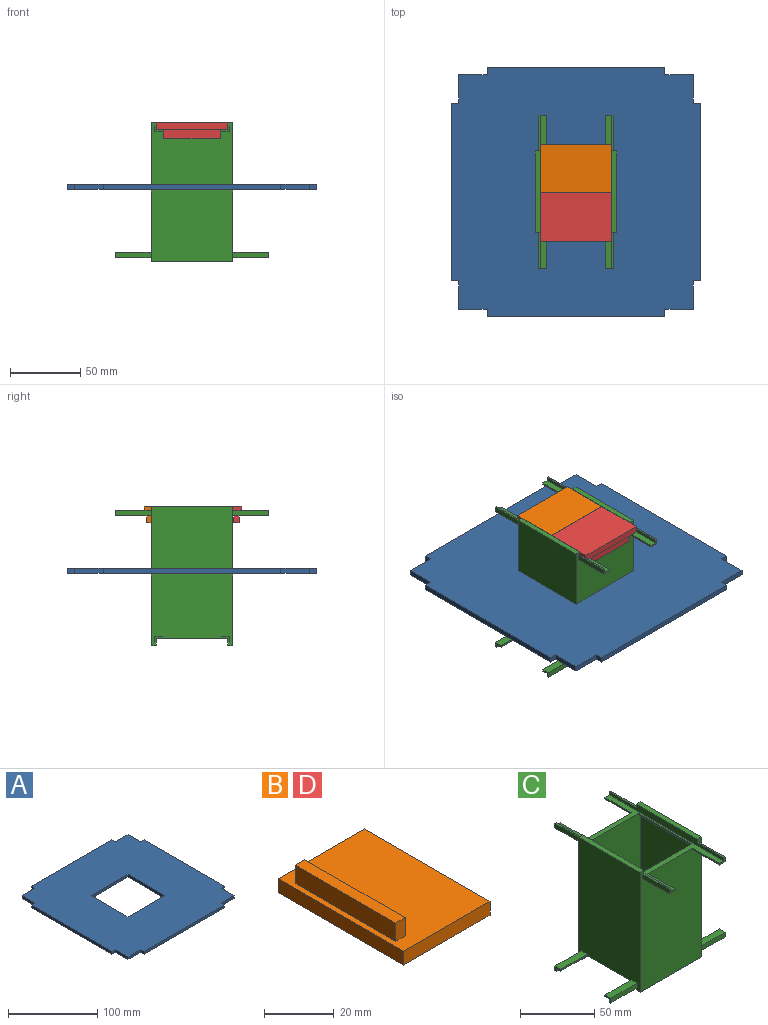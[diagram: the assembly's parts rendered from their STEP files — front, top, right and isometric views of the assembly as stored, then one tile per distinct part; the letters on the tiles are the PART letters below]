
ASSEMBLY  parts=4 mates=6
PART A: 26 faces, bbox 177.8x177.8x3.8 mm
  f0: plane 58.42x3.81mm, normal (0,1,0), area 222.6mm2, adj f1,f23,f24,f25
  f1: plane 58.42x3.81mm, normal (1,0,0), area 222.6mm2, adj f0,f2,f24,f25
  f2: plane 58.42x3.81mm, normal (0,-1,0), area 222.6mm2, adj f1,f23,f24,f25
  f3: plane 5.08x3.81mm, normal (0,-1,0), area 19.4mm2, adj f4,f22,f24,f25
  f4: plane 20.32x3.81mm, normal (-1,0,0), area 77.4mm2, adj f3,f5,f24,f25
  f5: plane 20.32x3.81mm, normal (0,-1,0), area 77.4mm2, adj f4,f6,f24,f25
  f6: plane 5.08x3.81mm, normal (-1,0,0), area 19.4mm2, adj f5,f7,f24,f25
  f7: plane 127x3.81mm, normal (0,-1,0), area 483.9mm2, adj f6,f8,f24,f25
  f8: plane 5.08x3.81mm, normal (1,0,0), area 19.4mm2, adj f7,f9,f24,f25
  f9: plane 20.32x3.81mm, normal (0,-1,0), area 77.4mm2, adj f8,f10,f24,f25
  f10: plane 20.32x3.81mm, normal (1,0,0), area 77.4mm2, adj f9,f11,f24,f25
  f11: plane 5.08x3.81mm, normal (0,-1,0), area 19.4mm2, adj f10,f12,f24,f25
  f12: plane 127x3.81mm, normal (1,0,0), area 483.9mm2, adj f11,f13,f24,f25
  f13: plane 5.08x3.81mm, normal (0,1,0), area 19.4mm2, adj f12,f14,f24,f25
  f14: plane 20.32x3.81mm, normal (1,0,0), area 77.4mm2, adj f13,f15,f24,f25
  f15: plane 20.32x3.81mm, normal (0,1,0), area 77.4mm2, adj f14,f16,f24,f25
  f16: plane 5.08x3.81mm, normal (1,0,0), area 19.4mm2, adj f15,f17,f24,f25
  f17: plane 127x3.81mm, normal (0,1,0), area 483.9mm2, adj f16,f18,f24,f25
  f18: plane 5.08x3.81mm, normal (-1,0,0), area 19.4mm2, adj f17,f19,f24,f25
  f19: plane 20.32x3.81mm, normal (0,1,0), area 77.4mm2, adj f18,f20,f24,f25
  f20: plane 20.32x3.81mm, normal (-1,0,0), area 77.4mm2, adj f19,f21,f24,f25
  f21: plane 5.08x3.81mm, normal (0,1,0), area 19.4mm2, adj f20,f22,f24,f25
  f22: plane 127x3.81mm, normal (-1,0,0), area 483.9mm2, adj f3,f21,f24,f25
  f23: plane 58.42x3.81mm, normal (-1,0,0), area 222.6mm2, adj f0,f2,f24,f25
  f24: plane 177.8x177.8mm, normal (0,0,1), area 27270.9mm2, adj f0,f1,f2,f3,f4,f5,f6,f7
  f25: plane 177.8x177.8mm, normal (0,0,-1), area 27270.9mm2, adj f0,f1,f2,f3,f4,f5,f6,f7
PART B: 11 faces, bbox 34.9x50.8x11.2 mm
  f0: plane 40.64x6.35mm, normal (1,0,0), area 258.1mm2, adj f1,f7,f9,f10
  f1: plane 40.64x3.81mm, normal (0,0,1), area 154.8mm2, adj f0,f4,f9,f10
  f2: plane 34.93x4.83mm, normal (0,-1,0), area 168.5mm2, adj f5,f6,f7,f8
  f3: plane 34.93x4.83mm, normal (0,1,0), area 168.5mm2, adj f5,f6,f7,f8
  f4: plane 40.64x6.35mm, normal (-1,0,0), area 258.1mm2, adj f1,f7,f9,f10
  f5: plane 50.8x4.83mm, normal (-1,0,0), area 245.2mm2, adj f2,f3,f7,f8
  f6: plane 50.8x4.83mm, normal (1,0,0), area 245.2mm2, adj f2,f3,f7,f8
  f7: plane 50.8x34.93mm, normal (0,0,1), area 1619.4mm2, adj f0,f2,f3,f4,f5,f6,f9,f10
  f8: plane 50.8x34.93mm, normal (0,0,-1), area 1774.2mm2, adj f2,f3,f5,f6
  f9: plane 6.35x3.81mm, normal (0,1,0), area 24.2mm2, adj f0,f1,f4,f7
  f10: plane 6.35x3.81mm, normal (0,-1,0), area 24.2mm2, adj f0,f1,f4,f7
PART C: 66 faces, bbox 109.2x109.2x99.1 mm
  f0: plane 99.06x58.42mm, normal (0,-1,0), area 5508.4mm2, adj f2,f3,f9,f10,f11,f14,f15,f16
  f1: plane 99.06x58.42mm, normal (0,1,0), area 5508.4mm2, adj f2,f3,f9,f10,f11,f14,f15,f17
  f2: plane 99.06x58.42mm, normal (-1,0,0), area 5508.4mm2, adj f0,f1,f5,f6,f13,f14,f16,f17
  f3: plane 99.06x58.42mm, normal (1,0,0), area 5508.4mm2, adj f0,f1,f5,f6,f13,f15,f16,f17
  f4: plane 87.63x50.8mm, normal (-1,0,0), area 4448.4mm2, adj f7,f8,f13,f20,f22,f23,f24,f25
  f5: plane 109.22x5.08mm, normal (0,1,0), area 425.8mm2, adj f2,f3,f13,f16,f26,f30,f43,f45
  f6: plane 109.22x5.08mm, normal (0,-1,0), area 425.8mm2, adj f2,f3,f13,f17,f33,f35,f36,f40
  f7: plane 87.63x50.8mm, normal (0,-1,0), area 4447.7mm2, adj f4,f10,f12,f18,f19,f20,f21,f22
  f8: plane 87.63x50.8mm, normal (0,1,0), area 4447.7mm2, adj f4,f10,f12,f18,f19,f20,f21,f24
  f9: plane 109.22x5.08mm, normal (1,0,0), area 425.8mm2, adj f0,f1,f10,f14,f54,f55,f56,f60
  f10: plane 109.22x50.8mm, normal (0,0,1), area 980.6mm2, adj f0,f1,f7,f8,f9,f11,f19,f21
  f11: plane 109.22x5.08mm, normal (-1,0,0), area 425.8mm2, adj f0,f1,f10,f15,f46,f50,f64,f65
  f12: plane 87.63x50.8mm, normal (1,0,0), area 4448.4mm2, adj f7,f8,f13,f18,f22,f23,f24,f25
  f13: plane 109.22x50.8mm, normal (0,0,-1), area 954.8mm2, adj f2,f3,f4,f5,f6,f12,f23,f25
  f14: plane 58.42x3.81mm, normal (0,0,1), area 222.6mm2, adj f0,f1,f2,f9
  f15: plane 58.42x3.81mm, normal (0,0,1), area 222.6mm2, adj f0,f1,f3,f11
  f16: plane 58.42x3.81mm, normal (0,0,-1), area 222.6mm2, adj f0,f2,f3,f5
  f17: plane 58.42x3.81mm, normal (0,0,-1), area 222.6mm2, adj f1,f2,f3,f6
  f18: plane 50.8x1.78mm, normal (0,0,-1), area 90.3mm2, adj f7,f8,f12,f19
  f19: plane 50.8x1.27mm, normal (1,0,0), area 64.5mm2, adj f7,f8,f10,f18
  f20: plane 50.8x1.27mm, normal (0,0,-1), area 64.5mm2, adj f4,f7,f8,f21
  f21: plane 50.8x1.27mm, normal (-1,0,0), area 64.5mm2, adj f7,f8,f10,f20
  f22: plane 50.8x1.27mm, normal (0,0,1), area 64.5mm2, adj f4,f7,f12,f23
  f23: plane 50.8x1.27mm, normal (0,-1,0), area 64.5mm2, adj f4,f12,f13,f22
  f24: plane 50.8x1.27mm, normal (0,0,1), area 64.5mm2, adj f4,f8,f12,f25
  f25: plane 50.8x1.27mm, normal (0,1,0), area 64.5mm2, adj f4,f12,f13,f24
  f26: plane 25.4x1.27mm, normal (0,0,-1), area 32.3mm2, adj f3,f5,f29,f30
  f27: plane 25.4x1.27mm, normal (0,1,0), area 32.3mm2, adj f3,f13,f28,f30
  f28: plane 25.4x5.59mm, normal (0,0,1), area 141.9mm2, adj f3,f27,f29,f30
  f29: plane 25.4x3.81mm, normal (0,-1,0), area 96.8mm2, adj f3,f26,f28,f30
  f30: plane 5.59x3.81mm, normal (1,0,0), area 10.3mm2, adj f5,f13,f26,f27,f28,f29
  f31: plane 25.4x5.59mm, normal (0,0,1), area 141.9mm2, adj f3,f32,f34,f35
  f32: plane 25.4x1.27mm, normal (0,-1,0), area 32.3mm2, adj f3,f13,f31,f35
  f33: plane 25.4x1.27mm, normal (0,0,-1), area 32.3mm2, adj f3,f6,f34,f35
  f34: plane 25.4x3.81mm, normal (0,1,0), area 96.8mm2, adj f3,f31,f33,f35
  f35: plane 5.59x3.81mm, normal (1,0,0), area 10.3mm2, adj f6,f13,f31,f32,f33,f34
  f36: plane 25.4x1.27mm, normal (0,0,-1), area 32.3mm2, adj f2,f6,f39,f40
  f37: plane 25.4x1.27mm, normal (0,-1,0), area 32.3mm2, adj f2,f13,f38,f40
  f38: plane 25.4x5.59mm, normal (0,0,1), area 141.9mm2, adj f2,f37,f39,f40
  f39: plane 25.4x3.81mm, normal (0,1,0), area 96.8mm2, adj f2,f36,f38,f40
  f40: plane 5.59x3.81mm, normal (-1,0,0), area 10.3mm2, adj f6,f13,f36,f37,f38,f39
  f41: plane 25.4x5.59mm, normal (0,0,1), area 141.9mm2, adj f2,f42,f44,f45
  f42: plane 25.4x1.27mm, normal (0,1,0), area 32.3mm2, adj f2,f13,f41,f45
  f43: plane 25.4x1.27mm, normal (0,0,-1), area 32.3mm2, adj f2,f5,f44,f45
  f44: plane 25.4x3.81mm, normal (0,-1,0), area 96.8mm2, adj f2,f41,f43,f45
  f45: plane 5.59x3.81mm, normal (-1,0,0), area 10.3mm2, adj f5,f13,f41,f42,f43,f44
  f46: plane 25.4x1.27mm, normal (0,0,1), area 32.3mm2, adj f1,f11,f47,f50
  f47: plane 25.4x3.81mm, normal (1,0,0), area 96.8mm2, adj f1,f46,f48,f50
  f48: plane 25.4x5.59mm, normal (0,0,-1), area 141.9mm2, adj f1,f47,f49,f50
  f49: plane 25.4x1.27mm, normal (-1,0,0), area 32.3mm2, adj f1,f10,f48,f50
  f50: plane 5.59x3.81mm, normal (0,1,0), area 10.3mm2, adj f10,f11,f46,f47,f48,f49
  f51: plane 25.4x1.27mm, normal (1,0,0), area 32.3mm2, adj f1,f10,f52,f55
  f52: plane 25.4x5.59mm, normal (0,0,-1), area 141.9mm2, adj f1,f51,f53,f55
  f53: plane 25.4x3.81mm, normal (-1,0,0), area 96.8mm2, adj f1,f52,f54,f55
  f54: plane 25.4x1.27mm, normal (0,0,1), area 32.3mm2, adj f1,f9,f53,f55
  f55: plane 5.59x3.81mm, normal (0,1,0), area 10.3mm2, adj f9,f10,f51,f52,f53,f54
  f56: plane 25.4x1.27mm, normal (0,0,1), area 32.3mm2, adj f0,f9,f57,f60
  f57: plane 25.4x3.81mm, normal (-1,0,0), area 96.8mm2, adj f0,f56,f58,f60
  f58: plane 25.4x5.59mm, normal (0,0,-1), area 141.9mm2, adj f0,f57,f59,f60
  f59: plane 25.4x1.27mm, normal (1,0,0), area 32.3mm2, adj f0,f10,f58,f60
  f60: plane 5.59x3.81mm, normal (0,-1,0), area 10.3mm2, adj f9,f10,f56,f57,f58,f59
  f61: plane 25.4x1.27mm, normal (-1,0,0), area 32.3mm2, adj f0,f10,f62,f65
  f62: plane 25.4x5.59mm, normal (0,0,-1), area 141.9mm2, adj f0,f61,f63,f65
  f63: plane 25.4x3.81mm, normal (1,0,0), area 96.8mm2, adj f0,f62,f64,f65
  f64: plane 25.4x1.27mm, normal (0,0,1), area 32.3mm2, adj f0,f11,f63,f65
  f65: plane 5.59x3.81mm, normal (0,-1,0), area 10.3mm2, adj f10,f11,f61,f62,f63,f64
PART D: same geometry as B
PLACE A t=(-107.8,105.97,43.78)mm
PLACE B rot(axis=(0.71,-0.71,0),180deg) t=(6.5,51.23,91.24)mm
PLACE C t=(-18.9,17.07,-2.49)mm fixed
PLACE D rot(axis=(0.71,0.71,0),180deg) t=(-44.3,-18.41,91.24)mm
MATE planar B.f7 <-> C.f10  axis (0,0,-1) through (-18.9,32.46,86.41)mm
MATE planar C.f3 <-> A.f23  axis (1,0,0) through (10.31,17.07,44.33)mm
MATE planar C.f0 <-> A.f0  axis (0,-1,0) through (-18.9,-12.14,39.6)mm
MATE planar C.f12 <-> D.f2  axis (1,0,0) through (-44.3,17.07,41.36)mm
MATE planar C.f11 <-> B.f2  axis (-1,0,0) through (6.5,17.07,88.57)mm
MATE planar D.f7 <-> C.f10  axis (0,0,-1) through (-18.9,0.36,86.41)mm
